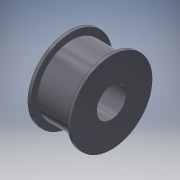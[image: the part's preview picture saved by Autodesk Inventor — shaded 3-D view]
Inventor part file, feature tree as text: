
AUTODESK INVENTOR PART (.ipt)
format: ipt  version: 2016 (Build 200138000, 138)  size: 128,512 bytes
history: native  units: mm
features: revolve x1, sketch x1
ambient origin geometry x8: Origin, YZ Plane, XZ Plane, XY Plane, X Axis, Y Axis, Z Axis, Center Point
bodies: Body1 (feature_tree)
feature tree (2):
  revolve  "Revolution1"  [1 undecoded]
  sketch  "Sketch2"  dims[d11=20.0mm d12=55.0mm d13=2.0mm d14=29.0mm d15=46.0mm d16=90.0deg]
note: 1 required parameter value undecoded (feature->parameter linkage not recoverable at this tier; creation-order binding heuristic only, values carry confidence <= 0.55)
